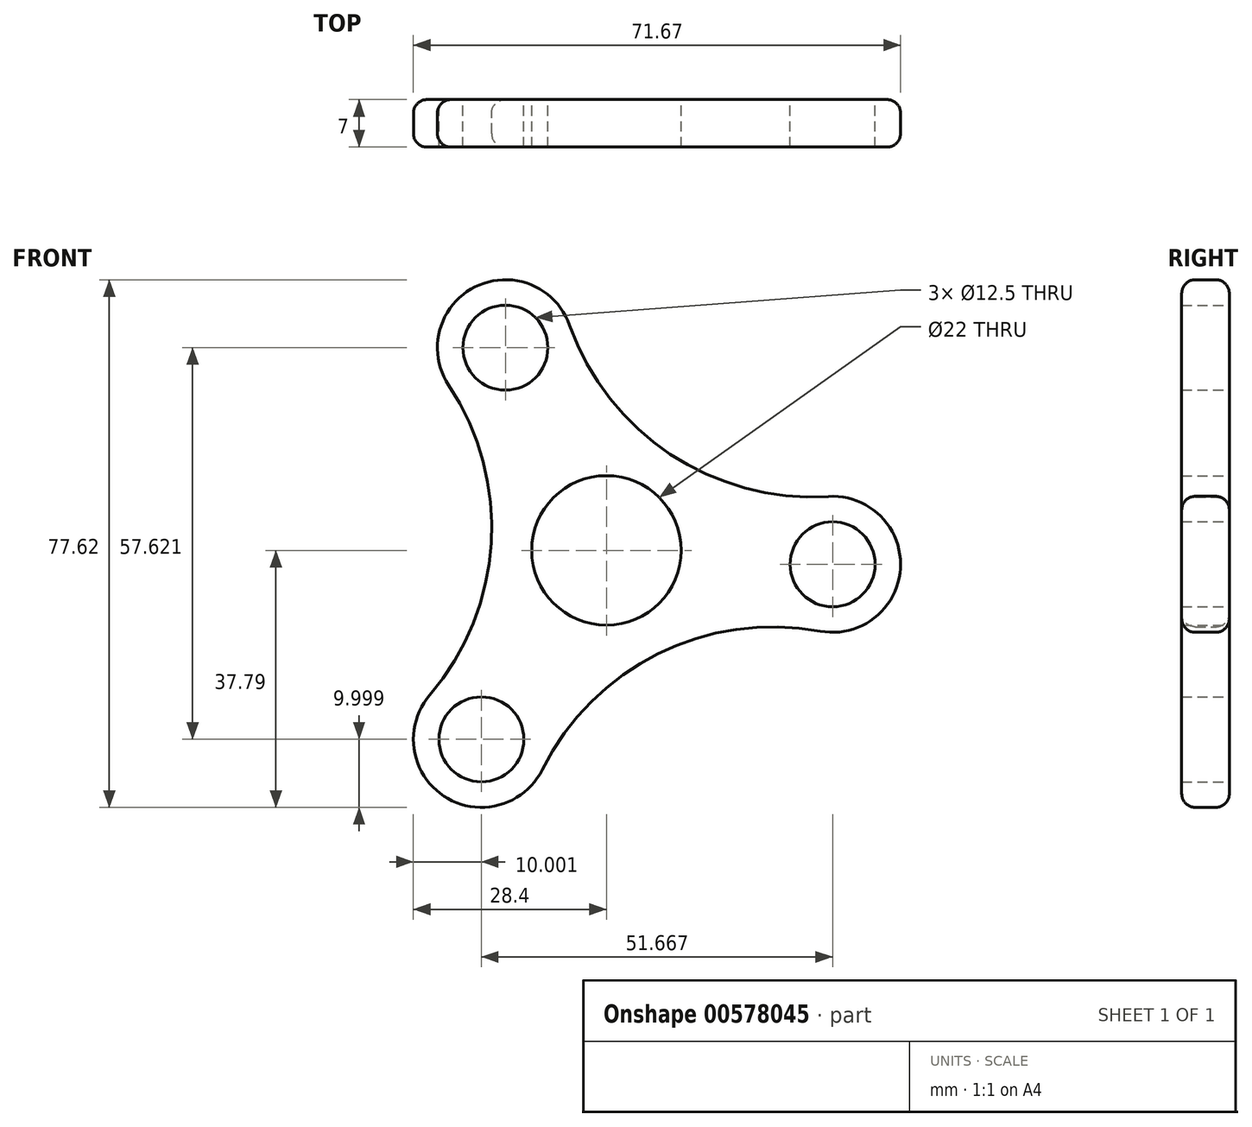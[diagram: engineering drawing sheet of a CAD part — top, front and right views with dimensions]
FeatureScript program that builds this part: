
annotation { "Feature Type Name" : "Feature", "Feature Type Description" : "" }
export const myFeature = defineFeature(function(context is Context, id is Id, definition is map)
    precondition{}
    {
        {
            var Q0;
            Q0=qCreatedBy(makeId("Front.planeOp"),FACE);
            var sketch = newSketch(context, id + "F0", { "sketchPlane" : qUnion([Q0])});
            skCircle(sketch, "E0.cCircle", {"center": v(0, 0) * mm, "radius": 25.98 * mm, "construction": true});
            skPoint(sketch, "E0.0.midPoint", {"position": v(16.07, 20.41) * mm});
            skPoint(sketch, "E1.visualSharp", {"position": v(51.43, -7.43) * mm});
            skArc(sketch, "E1.filletArc", {"start": v(31.44, -11.87) * mm, "mid": v(43.25, -2.65) * mm, "end": v(32.65, 7.94) * mm});
            skPoint(sketch, "E2.visualSharp", {"position": v(-19.28, 48.25) * mm});
            skArc(sketch, "E2.filletArc", {"start": v(-5.44, 33.16) * mm, "mid": v(-19.33, 38.78) * mm, "end": v(-23.2, 24.3) * mm});
            skPoint(sketch, "E3.visualSharp", {"position": v(-32.15, -40.82) * mm});
            skArc(sketch, "E3.filletArc", {"start": v(-26, -21.3) * mm, "mid": v(-23.92, -36.13) * mm, "end": v(-9.45, -32.25) * mm});
            skCircle(sketch, "E4", {"center": v(0, 0) * mm, "radius": 11 * mm});
            skCircle(sketch, "E5", {"center": v(-18.4, -27.8) * mm, "radius": 6.25 * mm});
            skCircle(sketch, "E6", {"center": v(33.27, -2.04) * mm, "radius": 6.25 * mm});
            skCircle(sketch, "E7", {"center": v(-14.87, 29.83) * mm, "radius": 6.25 * mm});
            skArc(sketch, "E8", {"start": v(-5.44, 33.16) * mm, "mid": v(9.38, 14.17) * mm, "end": v(32.65, 7.94) * mm});
            skArc(sketch, "E9", {"start": v(31.44, -11.87) * mm, "mid": v(7.58, -15.21) * mm, "end": v(-9.45, -32.25) * mm});
            skArc(sketch, "E10", {"start": v(-26, -21.3) * mm, "mid": v(-16.97, 1.04) * mm, "end": v(-23.2, 24.3) * mm});
            skCircle(sketch, "E11", {"center": v(0, 0) * mm, "radius": 33.33 * mm, "construction": true});
            skSolve(sketch);
        }
        {
            var Q0;
            Q0=makeQuery(id+"F0.imprint","IMPRINT",FACE,{"disambiguationData":[TD([[makeQuery(id+"F0.imprint","IMPRINT",EDGE,{"derivedFrom":sQuery(id+"F0.wireOp",EDGE,"E1.filletArc")}),1.0]])]});
            extrude(context, id + "F1", {"entities" : qUnion([Q0]), "depth" : 7 * mm, "offsetDistance" : 25 * mm});
        }
        {
            var Q0;
            Q0=makeQuery(id+"F1.opExtrude","CAP_EDGE",EDGE,{"disambiguationData":[OSD([sQuery(id+"F0.wireOp",EDGE,"E10")])],"isStart":false});
            var Q1;
            Q1=makeQuery(id+"F1.opExtrude","CAP_EDGE",EDGE,{"disambiguationData":[OSD([sQuery(id+"F0.wireOp",EDGE,"E9")])],"isStart":true});
            fillet(context, id + "F2", {"entities" : qUnion([Q0, Q1]), "radius" : 2 * mm, "tangentPropagation" : true, "allowEdgeOverflow" : false});
        }
    });
